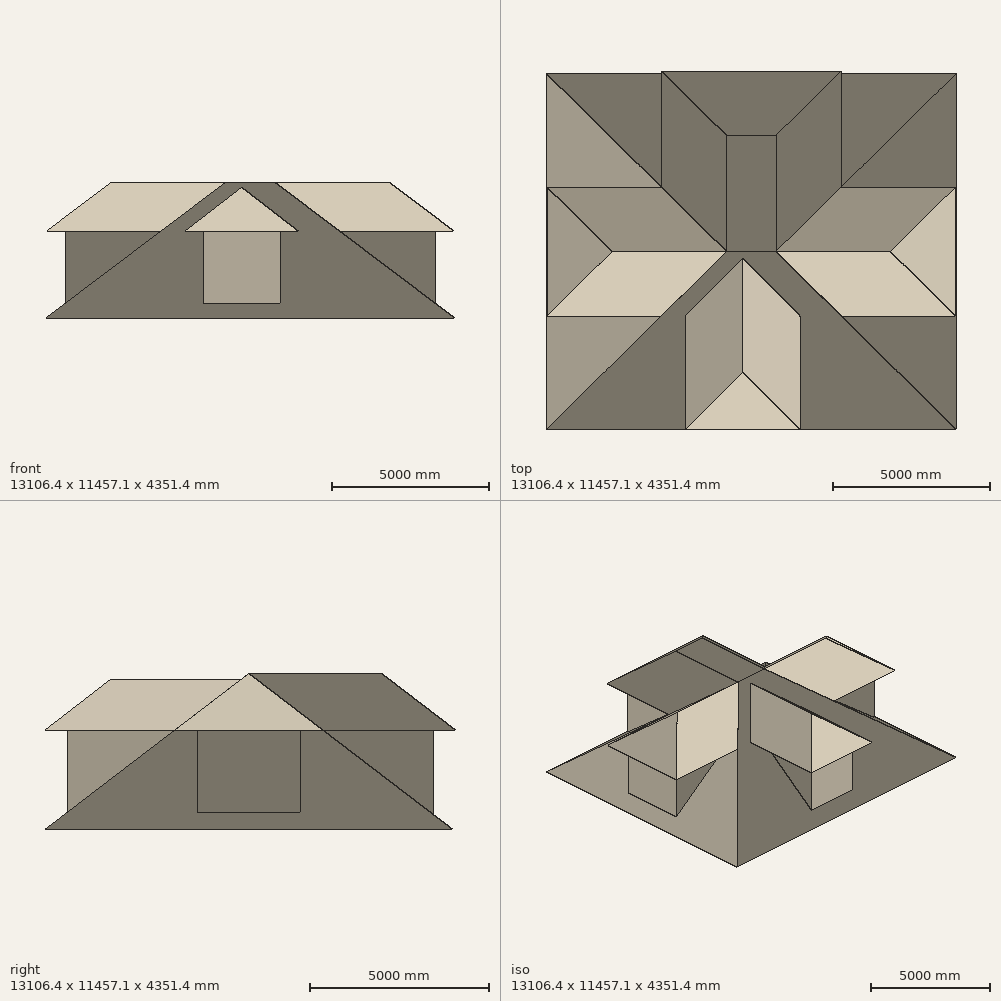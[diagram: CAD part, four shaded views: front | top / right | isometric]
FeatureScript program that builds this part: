
annotation { "Feature Type Name" : "Feature", "Feature Type Description" : "" }
export const myFeature = defineFeature(function(context is Context, id is Id, definition is map)
    precondition{}
    {
        {
            var Q0;
            Q0=qCreatedBy(makeId("Top.planeOp"),FACE);
            var sketch = newSketch(context, id + "F0", { "sketchPlane" : qUnion([Q0])});
            skLineSegment(sketch, "E0.bottom", {"start": v(6553.2, -5689.6) * mm, "end": v(-6553.2, -5689.6) * mm});
            skLineSegment(sketch, "E0.top", {"start": v(6553.2, 5689.6) * mm, "end": v(-6553.2, 5689.6) * mm});
            skLineSegment(sketch, "E0.left", {"start": v(6553.2, -5689.6) * mm, "end": v(6553.2, 5689.6) * mm});
            skLineSegment(sketch, "E0.right", {"start": v(-6553.2, -5689.6) * mm, "end": v(-6553.2, 5689.6) * mm});
            skPoint(sketch, "E0.middle", {"position": v(0, 0) * mm});
            skSolve(sketch);
        }
        {
            var Q0;
            Q0=qCreatedBy(makeId("Front.planeOp"),FACE);
            cPlane(context, id + "F1", {"entities" : qUnion([Q0]), "cplaneType" : CPlaneType.OFFSET, "offset" : 0 * mm, "width" : 152.4 * mm, "height" : 152.4 * mm});
        }
        {
            var Q0;
            Q0=qCreatedBy(makeId("Right.planeOp"),FACE);
            cPlane(context, id + "F2", {"entities" : qUnion([Q0]), "cplaneType" : CPlaneType.OFFSET, "offset" : 0 * mm, "width" : 152.4 * mm, "height" : 152.4 * mm});
        }
        {
            var Q0;
            Q0=qCreatedBy(makeId("Top.planeOp"),FACE);
            cPlane(context, id + "F3", {"entities" : qUnion([Q0]), "cplaneType" : CPlaneType.OFFSET, "offset" : 0 * mm, "width" : 152.4 * mm, "height" : 152.4 * mm});
        }
        {
            var Q0;
            Q0=qCreatedBy(id+"F3.planeOp",FACE);
            cPlane(context, id + "F4", {"entities" : qUnion([Q0]), "cplaneType" : CPlaneType.OFFSET, "offset" : 4351.35 * mm, "width" : 152.4 * mm, "height" : 152.4 * mm});
        }
        {
            var Q0;
            Q0=qCreatedBy(id+"F4.planeOp",FACE);
            var sketch = newSketch(context, id + "F5", { "sketchPlane" : qUnion([Q0])});
            skLineSegment(sketch, "E1", {"start": v(-787.4, 0) * mm, "end": v(787.4, 0) * mm});
            skLineSegment(sketch, "E2", {"start": v(0, 5179.24) * mm, "end": v(0, -2299.87) * mm, "construction": true});
            skSolve(sketch);
        }
        {
            var Q0;
            Q0=qCreatedBy(id+"F3.planeOp",FACE);
            var sketch = newSketch(context, id + "F6", { "sketchPlane" : qUnion([Q0])});
            skLineSegment(sketch, "E3.0", {"start": v(-787.4, 0) * mm, "end": v(787.4, 0) * mm, "construction": true});
            skSolve(sketch);
        }
        {
            var Q0;
            Q0=sQuery(id+"F6.wireOp",VERTEX,"E3.0.end");
            var Q1;
            Q1=sQuery(id+"F5.wireOp",VERTEX,"E1.end");
            var Q2;
            Q2=sQuery(id+"F0.wireOp",VERTEX,"E0.bottom.start");
            cPlane(context, id + "F7", {"entities" : qUnion([Q0, Q1, Q2]), "cplaneType" : CPlaneType.THREE_POINT, "offset" : 25.4 * mm, "width" : 152.4 * mm, "height" : 152.4 * mm});
        }
        {
            var Q0;
            Q0=sQuery(id+"F5.wireOp",VERTEX,"E1.end");
            var Q1;
            Q1=sQuery(id+"F6.wireOp",VERTEX,"E3.0.end");
            var Q2;
            Q2=sQuery(id+"F0.wireOp",VERTEX,"E0.top.start");
            cPlane(context, id + "F8", {"entities" : qUnion([Q0, Q1, Q2]), "cplaneType" : CPlaneType.THREE_POINT, "offset" : 25.4 * mm, "width" : 152.4 * mm, "height" : 152.4 * mm});
        }
        {
            var Q0;
            Q0=sQuery(id+"F5.wireOp",VERTEX,"E1.start");
            var Q1;
            Q1=sQuery(id+"F0.wireOp",VERTEX,"E0.top.end");
            var Q2;
            Q2=sQuery(id+"F6.wireOp",VERTEX,"E3.0.start");
            cPlane(context, id + "F9", {"entities" : qUnion([Q0, Q1, Q2]), "cplaneType" : CPlaneType.THREE_POINT, "offset" : 25.4 * mm, "width" : 152.4 * mm, "height" : 152.4 * mm});
        }
        {
            var Q0;
            Q0=sQuery(id+"F5.wireOp",VERTEX,"E1.start");
            var Q1;
            Q1=sQuery(id+"F6.wireOp",VERTEX,"E3.0.start");
            var Q2;
            Q2=sQuery(id+"F0.wireOp",VERTEX,"E0.bottom.end");
            cPlane(context, id + "F10", {"entities" : qUnion([Q0, Q1, Q2]), "cplaneType" : CPlaneType.THREE_POINT, "offset" : 25.4 * mm, "width" : 152.4 * mm, "height" : 152.4 * mm});
        }
        {
            var Q0;
            Q0=qCreatedBy(id+"F8.planeOp",FACE);
            var sketch = newSketch(context, id + "F11", { "sketchPlane" : qUnion([Q0])});
            skPoint(sketch, "E4.0", {"position": v(-560.47, 4351.35) * mm});
            skPoint(sketch, "E5.0", {"position": v(-8660.84, 0) * mm});
            skLineSegment(sketch, "E6", {"start": v(-560.47, 4351.35) * mm, "end": v(-8660.84, 0) * mm});
            skSolve(sketch);
        }
        {
            var Q0;
            Q0=qCreatedBy(id+"F9.planeOp",FACE);
            var sketch = newSketch(context, id + "F12", { "sketchPlane" : qUnion([Q0])});
            skPoint(sketch, "E7.0", {"position": v(560.47, 4351.35) * mm});
            skPoint(sketch, "E8.0", {"position": v(8660.84, 0) * mm});
            skLineSegment(sketch, "E9", {"start": v(560.47, 4351.35) * mm, "end": v(8660.84, 0) * mm});
            skSolve(sketch);
        }
        {
            var Q0;
            Q0=qCreatedBy(id+"F10.planeOp",FACE);
            var sketch = newSketch(context, id + "F13", { "sketchPlane" : qUnion([Q0])});
            skPoint(sketch, "E10.0", {"position": v(-560.47, 4351.35) * mm});
            skPoint(sketch, "E11.0", {"position": v(-8660.84, 0) * mm});
            skLineSegment(sketch, "E12", {"start": v(-8660.84, 0) * mm, "end": v(-560.47, 4351.35) * mm});
            skSolve(sketch);
        }
        {
            var Q0;
            Q0=qCreatedBy(id+"F7.planeOp",FACE);
            var sketch = newSketch(context, id + "F14", { "sketchPlane" : qUnion([Q0])});
            skPoint(sketch, "E13.0", {"position": v(560.47, 4351.35) * mm});
            skPoint(sketch, "E14.0", {"position": v(8660.84, 0) * mm});
            skLineSegment(sketch, "E15", {"start": v(560.47, 4351.35) * mm, "end": v(8660.84, 0) * mm});
            skSolve(sketch);
        }
        {
            var Q0;
            Q0=sQuery(id+"F0.wireOp",EDGE,"E0.bottom");
            var Q1;
            Q1=sQuery(id+"F5.wireOp",EDGE,"E1");
            loft(context, id + "F15", {"bodyType" : ToolBodyType.SURFACE, "wireProfilesArray" : [{ "wireProfileEntities" : qUnion([Q0]) }, { "wireProfileEntities" : qUnion([Q1]) }]});
        }
        {
            var Q0;
            Q0=sQuery(id+"F0.wireOp",EDGE,"E0.top");
            var Q1;
            Q1=sQuery(id+"F5.wireOp",EDGE,"E1");
            loft(context, id + "F16", {"bodyType" : ToolBodyType.SURFACE, "surfaceOperationType" : NewSurfaceOperationType.ADD, "wireProfilesArray" : [{ "wireProfileEntities" : qUnion([Q0]) }, { "wireProfileEntities" : qUnion([Q1]) }]});
        }
        {
            var Q0;
            Q0=sQuery(id+"F12.wireOp",EDGE,"E9");
            var Q1;
            Q1=sQuery(id+"F13.wireOp",EDGE,"E12");
            loft(context, id + "F17", {"bodyType" : ToolBodyType.SURFACE, "wireProfilesArray" : [{ "wireProfileEntities" : qUnion([Q0]) }, { "wireProfileEntities" : qUnion([Q1]) }]});
        }
        {
            var Q0;
            Q0=sQuery(id+"F11.wireOp",EDGE,"E6");
            var Q1;
            Q1=sQuery(id+"F14.wireOp",EDGE,"E15");
            loft(context, id + "F18", {"bodyType" : ToolBodyType.SURFACE, "wireProfilesArray" : [{ "wireProfileEntities" : qUnion([Q0]) }, { "wireProfileEntities" : qUnion([Q1]) }]});
        }
        {
            var Q0;
            Q0=qCreatedBy(id+"F4.planeOp",FACE);
            var sketch = newSketch(context, id + "F19", { "sketchPlane" : qUnion([Q0])});
            skPoint(sketch, "E16.0", {"position": v(-787.4, 0) * mm});
            skLineSegment(sketch, "E17.bottom", {"start": v(-787.4, 0) * mm, "end": v(787.4, 0) * mm});
            skLineSegment(sketch, "E17.top", {"start": v(-787.4, 3708.4) * mm, "end": v(787.4, 3708.4) * mm});
            skLineSegment(sketch, "E17.left", {"start": v(-787.4, 0) * mm, "end": v(-787.4, 3708.4) * mm});
            skLineSegment(sketch, "E17.right", {"start": v(787.4, 0) * mm, "end": v(787.4, 3708.4) * mm});
            skSolve(sketch);
        }
        {
            var Q0;
            Q0=qCreatedBy(id+"F8.planeOp",FACE);
            var sketch = newSketch(context, id + "F20", { "sketchPlane" : qUnion([Q0])});
            skLineSegment(sketch, "E18.0", {"start": v(-560.47, 4351.35) * mm, "end": v(-8660.84, 0) * mm, "construction": true});
            skPoint(sketch, "E19", {"position": v(-3492, 2776.6) * mm});
            skSolve(sketch);
        }
        {
            var Q0;
            Q0=sQuery(id+"F20.wireOp",VERTEX,"E19");
            var Q1;
            Q1=sQuery(id+"F0.wireOp",EDGE,"E0.top");
            cPlane(context, id + "F21", {"entities" : qUnion([Q0, Q1]), "cplaneType" : CPlaneType.LINE_POINT, "offset" : 25.4 * mm, "width" : 152.4 * mm, "height" : 152.4 * mm});
        }
        {
            var Q0;
            Q0=qCreatedBy(id+"F21.planeOp",FACE);
            var sketch = newSketch(context, id + "F22", { "sketchPlane" : qUnion([Q0])});
            skPoint(sketch, "E20.0", {"position": v(-2059.07, 2776.6) * mm});
            skLineSegment(sketch, "E21", {"start": v(-2059.07, 2776.6) * mm, "end": v(-5767.47, 2776.6) * mm});
            skSolve(sketch);
        }
        {
            var Q0;
            Q0=sQuery(id+"F22.wireOp",EDGE,"E21");
            var Q1;
            Q1=sQuery(id+"F19.wireOp",EDGE,"E17.right");
            var Q2;
            Q2=sQuery(id+"F19.wireOp",VERTEX,"E17.top.end");
            var Q3;
            Q3=sQuery(id+"F22.wireOp",VERTEX,"E21.end");
            loft(context, id + "F23", {"bodyType" : ToolBodyType.SURFACE, "wireProfilesArray" : [{ "wireProfileEntities" : qUnion([Q0]) }, { "wireProfileEntities" : qUnion([Q1]) }], "matchConnections" : true, "connections" : [{ "connectionEntities" : qUnion([Q2, Q3]), "connectionEdgeQueries" : qUnion([]), "connectionEdgeParameters" : [] }]});
        }
        {
            var Q0;
            Q0=makeQuery(id+"F23.opLoft","SWEPT_BODY",BODY,{"disambiguationData":[OSD([sQuery(id+"F19.wireOp",EDGE,"E17.right"),sQuery(id+"F22.wireOp",EDGE,"E21")])]});
            var Q1;
            Q1=qCreatedBy(id+"F2.planeOp",FACE);
            mirror(context, id + "F24", {"entities" : qUnion([Q0]), "mirrorPlane" : qUnion([Q1])});
        }
        {
            var Q0;
            Q0=makeQuery(id+"F23.opLoft","SWEPT_EDGE",EDGE,{"disambiguationData":[OSD([sQuery(id+"F19.wireOp",VERTEX,"E17.right.end"),sQuery(id+"F22.wireOp",VERTEX,"E21.end")])]});
            var Q1;
            Q1=makeQuery(id+"F24.opPattern","COPY",EDGE,{"derivedFrom":makeQuery(id+"F23.opLoft","SWEPT_EDGE",EDGE,{"disambiguationData":[OSD([sQuery(id+"F19.wireOp",VERTEX,"E17.right.end"),sQuery(id+"F22.wireOp",VERTEX,"E21.end")])]}),"instanceName":"1"});
            loft(context, id + "F25", {"bodyType" : ToolBodyType.SURFACE, "surfaceOperationType" : NewSurfaceOperationType.ADD, "wireProfilesArray" : [{ "wireProfileEntities" : qUnion([Q0]) }, { "wireProfileEntities" : qUnion([Q1]) }]});
        }
        {
            var Q0;
            Q0=makeQuery(id+"F23.opLoft","MID_CAP_EDGE",EDGE,{"disambiguationData":[OSD([sQuery(id+"F19.wireOp",VERTEX,"E17.right.start"),sQuery(id+"F19.wireOp",VERTEX,"E17.right.end"),sQuery(id+"F19.wireOp",EDGE,"E17.right")])],"capPos":1.0});
            var Q1;
            Q1=makeQuery(id+"F24.opPattern","COPY",EDGE,{"derivedFrom":makeQuery(id+"F23.opLoft","MID_CAP_EDGE",EDGE,{"disambiguationData":[OSD([sQuery(id+"F19.wireOp",VERTEX,"E17.right.start"),sQuery(id+"F19.wireOp",VERTEX,"E17.right.end"),sQuery(id+"F19.wireOp",EDGE,"E17.right")])],"capPos":1.0}),"instanceName":"1"});
            loft(context, id + "F26", {"bodyType" : ToolBodyType.SURFACE, "surfaceOperationType" : NewSurfaceOperationType.ADD, "wireProfilesArray" : [{ "wireProfileEntities" : qUnion([Q0]) }, { "wireProfileEntities" : qUnion([Q1]) }]});
        }
        {
            var Q0;
            Q0=makeQuery(id+"F23.opLoft","MID_CAP_EDGE",EDGE,{"disambiguationData":[OSD([sQuery(id+"F22.wireOp",VERTEX,"E21.start"),sQuery(id+"F22.wireOp",VERTEX,"E21.end"),sQuery(id+"F22.wireOp",EDGE,"E21")])],"capPos":0.0});
            var Q1;
            Q1=makeQuery(id+"F24.opPattern","COPY",EDGE,{"derivedFrom":makeQuery(id+"F23.opLoft","MID_CAP_EDGE",EDGE,{"disambiguationData":[OSD([sQuery(id+"F22.wireOp",VERTEX,"E21.start"),sQuery(id+"F22.wireOp",VERTEX,"E21.end"),sQuery(id+"F22.wireOp",EDGE,"E21")])],"capPos":0.0}),"instanceName":"1"});
            loft(context, id + "F27", {"bodyType" : ToolBodyType.SURFACE, "surfaceOperationType" : NewSurfaceOperationType.ADD, "wireProfilesArray" : [{ "wireProfileEntities" : qUnion([Q0]) }, { "wireProfileEntities" : qUnion([Q1]) }]});
        }
        {
            var Q0;
            Q0=makeQuery(id+"F27.opLoft","SWEPT_FACE",FACE,{"disambiguationData":[OSD([sQuery(id+"F22.wireOp",VERTEX,"E21.start"),sQuery(id+"F22.wireOp",VERTEX,"E21.end"),sQuery(id+"F22.wireOp",EDGE,"E21")])]});
            var sketch = newSketch(context, id + "F28", { "sketchPlane" : qUnion([Q0])});
            skLineSegment(sketch, "E22.0", {"start": v(2874.05, 5767.47) * mm, "end": v(2874.05, 2059.07) * mm, "construction": true});
            skLineSegment(sketch, "E23.0", {"start": v(2874.05, 5767.47) * mm, "end": v(-2874.05, 5767.47) * mm, "construction": true});
            skLineSegment(sketch, "E24.0", {"start": v(-2874.05, 5767.47) * mm, "end": v(-2874.05, 2059.07) * mm, "construction": true});
            skLineSegment(sketch, "E25.0", {"start": v(2264.45, 5157.87) * mm, "end": v(2264.45, 2059.07) * mm});
            skLineSegment(sketch, "E26.0", {"start": v(2264.45, 5157.87) * mm, "end": v(-2264.45, 5157.87) * mm});
            skLineSegment(sketch, "E27.0", {"start": v(-2264.45, 5157.87) * mm, "end": v(-2264.45, 2059.07) * mm});
            skSolve(sketch);
        }
        {
            var Q0;
            Q0=sQuery(id+"F28.wireOp",EDGE,"E26.0");
            var Q1;
            Q1=sQuery(id+"F28.wireOp",EDGE,"E25.0");
            var Q2;
            Q2=sQuery(id+"F28.wireOp",EDGE,"E27.0");
            extrude(context, id + "F29", {"bodyType" : ToolBodyType.SURFACE, "surfaceEntities" : qUnion([Q0, Q1, Q2]), "endBound" : BoundingType.UP_TO_NEXT, "oppositeDirection" : true, "depth" : 25.4 * mm, "offsetDistance" : 25.4 * mm});
        }
        {
            var Q0;
            Q0=sQuery(id+"F20.wireOp",VERTEX,"E19");
            var Q1;
            Q1=sQuery(id+"F0.wireOp",EDGE,"E0.left");
            cPlane(context, id + "F30", {"entities" : qUnion([Q0, Q1]), "cplaneType" : CPlaneType.LINE_POINT, "offset" : 25.4 * mm, "width" : 152.4 * mm, "height" : 152.4 * mm});
        }
        {
            var Q0;
            Q0=qCreatedBy(id+"F30.planeOp",FACE);
            var sketch = newSketch(context, id + "F31", { "sketchPlane" : qUnion([Q0])});
            skPoint(sketch, "E28.0", {"position": v(-2874.05, 2776.6) * mm});
            skLineSegment(sketch, "E29", {"start": v(-2874.05, 2776.6) * mm, "end": v(-6531.65, 2776.6) * mm});
            skSolve(sketch);
        }
        {
            var Q0;
            Q0=qCreatedBy(id+"F1.planeOp",FACE);
            var sketch = newSketch(context, id + "F32", { "sketchPlane" : qUnion([Q0])});
            skPoint(sketch, "E30.0", {"position": v(787.4, 4351.35) * mm});
            skLineSegment(sketch, "E31", {"start": v(787.4, 4351.35) * mm, "end": v(4445, 4351.35) * mm});
            skSolve(sketch);
        }
        {
            var Q0;
            Q0=sQuery(id+"F31.wireOp",EDGE,"E29");
            var Q1;
            Q1=sQuery(id+"F32.wireOp",EDGE,"E31");
            var Q2;
            Q2=sQuery(id+"F31.wireOp",VERTEX,"E29.end");
            var Q3;
            Q3=sQuery(id+"F32.wireOp",VERTEX,"E31.end");
            loft(context, id + "F33", {"bodyType" : ToolBodyType.SURFACE, "wireProfilesArray" : [{ "wireProfileEntities" : qUnion([Q0]) }, { "wireProfileEntities" : qUnion([Q1]) }], "matchConnections" : true, "connections" : [{ "connectionEntities" : qUnion([Q2, Q3]), "connectionEdgeQueries" : qUnion([]), "connectionEdgeParameters" : [] }]});
        }
        {
            var Q0;
            Q0=makeQuery(id+"F33.opLoft","SWEPT_BODY",BODY,{"disambiguationData":[OSD([sQuery(id+"F31.wireOp",EDGE,"E29"),sQuery(id+"F32.wireOp",EDGE,"E31")])]});
            var Q1;
            Q1=qCreatedBy(id+"F1.planeOp",FACE);
            mirror(context, id + "F34", {"entities" : qUnion([Q0]), "mirrorPlane" : qUnion([Q1])});
        }
        {
            var Q0;
            Q0=makeQuery(id+"F33.opLoft","SWEPT_EDGE",EDGE,{"disambiguationData":[OSD([sQuery(id+"F31.wireOp",VERTEX,"E29.end"),sQuery(id+"F32.wireOp",VERTEX,"E31.end")])]});
            var Q1;
            Q1=makeQuery(id+"F34.opPattern","COPY",EDGE,{"derivedFrom":makeQuery(id+"F33.opLoft","SWEPT_EDGE",EDGE,{"disambiguationData":[OSD([sQuery(id+"F31.wireOp",VERTEX,"E29.end"),sQuery(id+"F32.wireOp",VERTEX,"E31.end")])]}),"instanceName":"1"});
            var Q2;
            Q2=makeQuery(id+"F34.opPattern","COPY",VERTEX,{"derivedFrom":makeQuery(id+"F33.opLoft","MID_CAP_VERTEX",VERTEX,{"disambiguationData":[OSD([sQuery(id+"F31.wireOp",VERTEX,"E29.end")])],"capPos":0.0}),"instanceName":"1"});
            var Q3;
            Q3=makeQuery(id+"F33.opLoft","MID_CAP_VERTEX",VERTEX,{"disambiguationData":[OSD([sQuery(id+"F31.wireOp",VERTEX,"E29.end")])],"capPos":0.0});
            loft(context, id + "F35", {"bodyType" : ToolBodyType.SURFACE, "surfaceOperationType" : NewSurfaceOperationType.ADD, "wireProfilesArray" : [{ "wireProfileEntities" : qUnion([Q0]) }, { "wireProfileEntities" : qUnion([Q1]) }], "matchConnections" : true, "connections" : [{ "connectionEntities" : qUnion([Q2, Q3]), "connectionEdgeQueries" : qUnion([]), "connectionEdgeParameters" : [] }]});
        }
        {
            var Q0;
            Q0=makeQuery(id+"F34.opPattern","COPY",EDGE,{"derivedFrom":makeQuery(id+"F33.opLoft","MID_CAP_EDGE",EDGE,{"disambiguationData":[OSD([sQuery(id+"F31.wireOp",VERTEX,"E29.start"),sQuery(id+"F31.wireOp",VERTEX,"E29.end"),sQuery(id+"F31.wireOp",EDGE,"E29")])],"capPos":0.0}),"instanceName":"1"});
            var Q1;
            Q1=makeQuery(id+"F33.opLoft","MID_CAP_EDGE",EDGE,{"disambiguationData":[OSD([sQuery(id+"F31.wireOp",VERTEX,"E29.start"),sQuery(id+"F31.wireOp",VERTEX,"E29.end"),sQuery(id+"F31.wireOp",EDGE,"E29")])],"capPos":0.0});
            loft(context, id + "F36", {"bodyType" : ToolBodyType.SURFACE, "surfaceOperationType" : NewSurfaceOperationType.ADD, "wireProfilesArray" : [{ "wireProfileEntities" : qUnion([Q0]) }, { "wireProfileEntities" : qUnion([Q1]) }]});
        }
        {
            var Q0;
            Q0=makeQuery(id+"F36.opLoft","SWEPT_FACE",FACE,{"disambiguationData":[OSD([sQuery(id+"F31.wireOp",VERTEX,"E29.start"),sQuery(id+"F31.wireOp",VERTEX,"E29.end"),sQuery(id+"F31.wireOp",EDGE,"E29")])]});
            var sketch = newSketch(context, id + "F37", { "sketchPlane" : qUnion([Q0])});
            skLineSegment(sketch, "E32.0", {"start": v(6531.65, 2059.07) * mm, "end": v(2874.05, 2059.07) * mm, "construction": true});
            skLineSegment(sketch, "E33.0", {"start": v(6531.65, 2059.07) * mm, "end": v(6531.65, -2059.07) * mm, "construction": true});
            skLineSegment(sketch, "E34.0", {"start": v(6531.65, -2059.07) * mm, "end": v(2874.05, -2059.07) * mm, "construction": true});
            skLineSegment(sketch, "E35.0", {"start": v(5922.05, 1449.47) * mm, "end": v(2874.05, 1449.47) * mm});
            skLineSegment(sketch, "E36.0", {"start": v(5922.05, 1449.47) * mm, "end": v(5922.05, -1449.47) * mm});
            skLineSegment(sketch, "E37.0", {"start": v(5922.05, -1449.47) * mm, "end": v(2874.05, -1449.47) * mm});
            skSolve(sketch);
        }
        {
            var Q0;
            Q0=sQuery(id+"F37.wireOp",EDGE,"E37.0");
            var Q1;
            Q1=sQuery(id+"F37.wireOp",EDGE,"E36.0");
            var Q2;
            Q2=sQuery(id+"F37.wireOp",EDGE,"E35.0");
            var Q3;
            Q3=makeQuery(id+"F18.opLoft","SWEPT_FACE",FACE,{"disambiguationData":[OSD([sQuery(id+"F11.wireOp",VERTEX,"E6.start"),sQuery(id+"F11.wireOp",VERTEX,"E6.end"),sQuery(id+"F11.wireOp",EDGE,"E6"),sQuery(id+"F14.wireOp",VERTEX,"E15.start"),sQuery(id+"F14.wireOp",VERTEX,"E15.end"),sQuery(id+"F14.wireOp",EDGE,"E15")])]});
            extrude(context, id + "F38", {"bodyType" : ToolBodyType.SURFACE, "surfaceEntities" : qUnion([Q0, Q1, Q2]), "endBound" : BoundingType.UP_TO_NEXT, "depth" : 25.4 * mm, "endBoundEntityFace" : qUnion([Q3]), "offsetDistance" : 25.4 * mm});
        }
        {
            var Q0;
            Q0=makeQuery(id+"F38.opExtrude","SWEPT_BODY",BODY,{"disambiguationData":[OSD([sQuery(id+"F37.wireOp",EDGE,"E35.0")])]});
            var Q1;
            Q1=makeQuery(id+"F33.opLoft","SWEPT_BODY",BODY,{"disambiguationData":[OSD([sQuery(id+"F31.wireOp",EDGE,"E29"),sQuery(id+"F32.wireOp",EDGE,"E31")])]});
            var Q2;
            Q2=qCreatedBy(id+"F2.planeOp",FACE);
            mirror(context, id + "F39", {"entities" : qUnion([Q0, Q1]), "mirrorPlane" : qUnion([Q2])});
        }
        {
            var Q0;
            Q0=qCreatedBy(id+"F2.planeOp",FACE);
            cPlane(context, id + "F40", {"entities" : qUnion([Q0]), "cplaneType" : CPlaneType.OFFSET, "offset" : 274.32 * mm, "oppositeDirection" : true, "width" : 152.4 * mm, "height" : 152.4 * mm});
        }
        {
            var Q0;
            Q0=makeQuery(id+"F39.opPattern","COPY",FACE,{"derivedFrom":makeQuery(id+"F36.opLoft","SWEPT_FACE",FACE,{"disambiguationData":[OSD([sQuery(id+"F31.wireOp",VERTEX,"E29.start"),sQuery(id+"F31.wireOp",VERTEX,"E29.end"),sQuery(id+"F31.wireOp",EDGE,"E29")])]}),"instanceName":"1"});
            var sketch = newSketch(context, id + "F41", { "sketchPlane" : qUnion([Q0])});
            skLineSegment(sketch, "E38", {"start": v(-274.32, 5689.6) * mm, "end": v(-274.32, 2059.07) * mm, "construction": true});
            skLineSegment(sketch, "E39.0", {"start": v(6553.2, 5689.6) * mm, "end": v(-6553.2, 5689.6) * mm, "construction": true});
            skLineSegment(sketch, "E40.0", {"start": v(-1493.52, 5080) * mm, "end": v(-1493.52, 2059.07) * mm});
            skLineSegment(sketch, "E41.0", {"start": v(944.88, 5080) * mm, "end": v(944.88, 2059.07) * mm});
            skLineSegment(sketch, "E42.0", {"start": v(944.88, 5080) * mm, "end": v(-1493.52, 5080) * mm});
            skLineSegment(sketch, "E43", {"start": v(-2874.05, 2059.07) * mm, "end": v(2874.05, 2059.07) * mm, "construction": true});
            skSolve(sketch);
        }
        {
            var Q0;
            Q0=sQuery(id+"F41.wireOp",EDGE,"E40.0");
            var Q1;
            Q1=sQuery(id+"F41.wireOp",EDGE,"E42.0");
            var Q2;
            Q2=sQuery(id+"F41.wireOp",EDGE,"E41.0");
            extrude(context, id + "F42", {"bodyType" : ToolBodyType.SURFACE, "surfaceEntities" : qUnion([Q0, Q1, Q2]), "endBound" : BoundingType.UP_TO_NEXT, "depth" : 25.4 * mm, "offsetDistance" : 25.4 * mm});
        }
        {
            var Q0;
            Q0=makeQuery(id+"F36.opLoft","SWEPT_FACE",FACE,{"disambiguationData":[OSD([sQuery(id+"F31.wireOp",VERTEX,"E29.start"),sQuery(id+"F31.wireOp",VERTEX,"E29.end"),sQuery(id+"F31.wireOp",EDGE,"E29")])]});
            var sketch = newSketch(context, id + "F43", { "sketchPlane" : qUnion([Q0])});
            skLineSegment(sketch, "E44", {"start": v(-1493.52, 5080) * mm, "end": v(-1493.52, 2059.07) * mm, "construction": true});
            skLineSegment(sketch, "E45", {"start": v(944.88, 5080) * mm, "end": v(-1493.52, 5080) * mm, "construction": true});
            skLineSegment(sketch, "E46", {"start": v(944.88, 2059.07) * mm, "end": v(944.88, 5080) * mm, "construction": true});
            skLineSegment(sketch, "E47.0", {"start": v(-2103.12, 5689.6) * mm, "end": v(-2103.12, 2059.07) * mm});
            skLineSegment(sketch, "E48.0", {"start": v(1554.48, 5689.6) * mm, "end": v(-2103.12, 5689.6) * mm});
            skLineSegment(sketch, "E49.0", {"start": v(1554.48, 2059.07) * mm, "end": v(1554.48, 5689.6) * mm});
            skLineSegment(sketch, "E50", {"start": v(-2874.05, 2059.07) * mm, "end": v(2874.05, 2059.07) * mm, "construction": true});
            skLineSegment(sketch, "E51", {"start": v(-2103.12, 2059.07) * mm, "end": v(-1493.52, 2059.07) * mm});
            skLineSegment(sketch, "E52", {"start": v(-1493.52, 5080) * mm, "end": v(944.88, 5080) * mm});
            skLineSegment(sketch, "E53", {"start": v(944.88, 2059.07) * mm, "end": v(1554.48, 2059.07) * mm});
            skLineSegment(sketch, "E54", {"start": v(944.88, 2059.07) * mm, "end": v(944.88, 5080) * mm});
            skLineSegment(sketch, "E55", {"start": v(-1493.52, 2059.07) * mm, "end": v(-1493.52, 5080) * mm});
            skSolve(sketch);
        }
        {
            var Q0;
            Q0=sQuery(id+"F43.wireOp",EDGE,"E49.0");
            var Q1;
            Q1=sQuery(id+"F43.wireOp",EDGE,"E47.0");
            loft(context, id + "F44", {"bodyType" : ToolBodyType.SURFACE, "wireProfilesArray" : [{ "wireProfileEntities" : qUnion([Q0]) }, { "wireProfileEntities" : qUnion([Q1]) }]});
        }
        {
            var Q0;
            Q0=makeQuery(id+"F44.opLoft","SWEPT_FACE",FACE,{"disambiguationData":[OSD([sQuery(id+"F43.wireOp",VERTEX,"E47.0.start"),sQuery(id+"F43.wireOp",VERTEX,"E47.0.end"),sQuery(id+"F43.wireOp",VERTEX,"E49.0.start"),sQuery(id+"F43.wireOp",VERTEX,"E49.0.end"),sQuery(id+"F43.wireOp",EDGE,"E47.0"),sQuery(id+"F43.wireOp",EDGE,"E49.0")])]});
            cPlane(context, id + "F45", {"entities" : qUnion([Q0]), "cplaneType" : CPlaneType.OFFSET, "offset" : 1413.5 * mm, "oppositeDirection" : true, "width" : 152.4 * mm, "height" : 152.4 * mm});
        }
        {
            var Q0;
            Q0=makeQuery(id+"F44.opLoft","MID_CAP_VERTEX",VERTEX,{"disambiguationData":[OSD([sQuery(id+"F43.wireOp",VERTEX,"E49.0.end")])],"capPos":0.0});
            var Q1;
            Q1=makeQuery(id+"F44.opLoft","MID_CAP_EDGE",EDGE,{"disambiguationData":[OSD([sQuery(id+"F43.wireOp",VERTEX,"E49.0.start"),sQuery(id+"F43.wireOp",VERTEX,"E49.0.end"),sQuery(id+"F43.wireOp",EDGE,"E49.0")])],"capPos":0.0});
            cPlane(context, id + "F46", {"entities" : qUnion([Q0, Q1]), "cplaneType" : CPlaneType.LINE_POINT, "offset" : 25.4 * mm, "width" : 152.4 * mm, "height" : 152.4 * mm});
        }
        {
            var Q0;
            Q0=qCreatedBy(id+"F46.planeOp",FACE);
            cPlane(context, id + "F47", {"entities" : qUnion([Q0]), "cplaneType" : CPlaneType.OFFSET, "offset" : 1828.8 * mm, "oppositeDirection" : true, "width" : 152.4 * mm, "height" : 152.4 * mm});
        }
        {
            var Q0;
            Q0=qCreatedBy(id+"F45.planeOp",FACE);
            var sketch = newSketch(context, id + "F48", { "sketchPlane" : qUnion([Q0])});
            skLineSegment(sketch, "E56", {"start": v(-274.32, 1524.52) * mm, "end": v(-274.32, -7434.52) * mm, "construction": true});
            skLineSegment(sketch, "E57", {"start": v(-9522.87, 3860.8) * mm, "end": v(5889.27, 3860.8) * mm, "construction": true});
            skLineSegment(sketch, "E58", {"start": v(-1001.06, 210.84) * mm, "end": v(1001.06, 210.84) * mm, "construction": true});
            skLineSegment(sketch, "E59", {"start": v(-274.32, 210.84) * mm, "end": v(-274.32, 3860.8) * mm});
            skSolve(sketch);
        }
        {
            var Q0;
            Q0=makeQuery(id+"F44.opLoft","MID_CAP_EDGE",EDGE,{"disambiguationData":[OSD([sQuery(id+"F43.wireOp",VERTEX,"E49.0.start"),sQuery(id+"F43.wireOp",VERTEX,"E49.0.end"),sQuery(id+"F43.wireOp",EDGE,"E49.0")])],"capPos":0.0});
            var Q1;
            Q1=sQuery(id+"F48.wireOp",EDGE,"E59");
            var Q2;
            Q2=sQuery(id+"F48.wireOp",VERTEX,"E59.end");
            var Q3;
            Q3=makeQuery(id+"F44.opLoft","MID_CAP_VERTEX",VERTEX,{"disambiguationData":[OSD([sQuery(id+"F43.wireOp",VERTEX,"E49.0.end")])],"capPos":0.0});
            loft(context, id + "F49", {"bodyType" : ToolBodyType.SURFACE, "surfaceOperationType" : NewSurfaceOperationType.ADD, "wireProfilesArray" : [{ "wireProfileEntities" : qUnion([Q0]) }, { "wireProfileEntities" : qUnion([Q1]) }], "matchConnections" : true, "connections" : [{ "connectionEntities" : qUnion([Q2, Q3]), "connectionEdgeQueries" : qUnion([]), "connectionEdgeParameters" : [] }]});
        }
        {
            var Q0;
            Q0=makeQuery(id+"F44.opLoft","SWEPT_BODY",BODY,{"disambiguationData":[OSD([sQuery(id+"F43.wireOp",EDGE,"E47.0"),sQuery(id+"F43.wireOp",EDGE,"E49.0")])]});
            var Q1;
            Q1=qCreatedBy(id+"F40.planeOp",FACE);
            mirror(context, id + "F50", {"entities" : qUnion([Q0]), "mirrorPlane" : qUnion([Q1])});
        }
        {
            var Q0;
            Q0=makeQuery(id+"F49.opLoft","SWEPT_EDGE",EDGE,{"disambiguationData":[OSD([sQuery(id+"F43.wireOp",VERTEX,"E49.0.end"),sQuery(id+"F48.wireOp",VERTEX,"E59.end")])]});
            var Q1;
            Q1=makeQuery(id+"F50.opPattern","COPY",EDGE,{"derivedFrom":makeQuery(id+"F49.opLoft","SWEPT_EDGE",EDGE,{"disambiguationData":[OSD([sQuery(id+"F43.wireOp",VERTEX,"E49.0.end"),sQuery(id+"F48.wireOp",VERTEX,"E59.end")])]}),"instanceName":"1"});
            var Q2;
            Q2=makeQuery(id+"F44.opLoft","MID_CAP_VERTEX",VERTEX,{"disambiguationData":[OSD([sQuery(id+"F43.wireOp",VERTEX,"E47.0.start")])],"capPos":1.0});
            var Q3;
            {var subQ0=sQuery(id+"F43.wireOp",VERTEX,"E49.0.end");Q3=makeQuery(id+"F49.join.opBoolean","MERGE",VERTEX,{"derivedFrom":[makeQuery(id+"F44.opLoft","MID_CAP_VERTEX",VERTEX,{"disambiguationData":[OSD([subQ0])],"capPos":0.0}),makeQuery(id+"F49.opLoft","MID_CAP_VERTEX",VERTEX,{"disambiguationData":[OSD([subQ0])],"capPos":0.0})]});}
            loft(context, id + "F51", {"bodyType" : ToolBodyType.SURFACE, "surfaceOperationType" : NewSurfaceOperationType.ADD, "wireProfilesArray" : [{ "wireProfileEntities" : qUnion([Q0]) }, { "wireProfileEntities" : qUnion([Q1]) }], "matchConnections" : true, "connections" : [{ "connectionEntities" : qUnion([Q2, Q3]), "connectionEdgeQueries" : qUnion([]), "connectionEdgeParameters" : [] }]});
        }
    });
